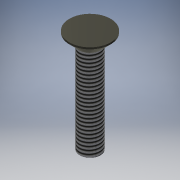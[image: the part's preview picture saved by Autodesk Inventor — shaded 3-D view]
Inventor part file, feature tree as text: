
AUTODESK INVENTOR PART (.ipt)
format: ipt  version: 2016 (Build 200138000, 138)  size: 135,168 bytes
history: native  units: mm
features: extrude x5, sketch x5, other x1, thread x1, chamfer x1
ambient origin geometry x1: Origin
bodies: Body1 (feature_tree)
feature tree (13):
  other  "ソリッド1"
  extrude  "押し出し1"  Depth=3.0mm
  extrude  "押し出し2"  Depth=6.0mm TaperAngle=0.0deg
  thread  "ねじ1"
  chamfer  "面取り1"  Distance=6.0mm
  extrude  "押し出し4"  Depth=1.75mm TaperAngle=0.0deg
  extrude  "押し出し5"  Depth=10.0mm TaperAngle=0.0deg
  extrude  "押し出し6"  Depth=1.5mm TaperAngle=45.0deg
  sketch  "スケッチ1"
  sketch  "スケッチ2"
  sketch  "スケッチ4"
  sketch  "スケッチ5"
  sketch  "スケッチ6"
